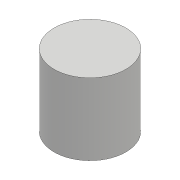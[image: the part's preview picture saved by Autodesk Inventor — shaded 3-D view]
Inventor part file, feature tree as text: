
AUTODESK INVENTOR PART (.ipt)
format: ipt  version: 2017 (Build 210142000, 142)  size: 71,168 bytes
history: native  units: mm
features: extrude x1, sketch x1
ambient origin geometry x8: Origin, YZ Plane, XZ Plane, XY Plane, X Axis, Y Axis, Z Axis, Center Point
bodies: Solid1 (feature_tree)
feature tree (2):
  extrude  "Extrusion1"  Depth=10.0mm TaperAngle=0.0deg
  sketch  "Sketch1"  dims[d0=10.0mm d1=10.0mm d2=0.0mm]
